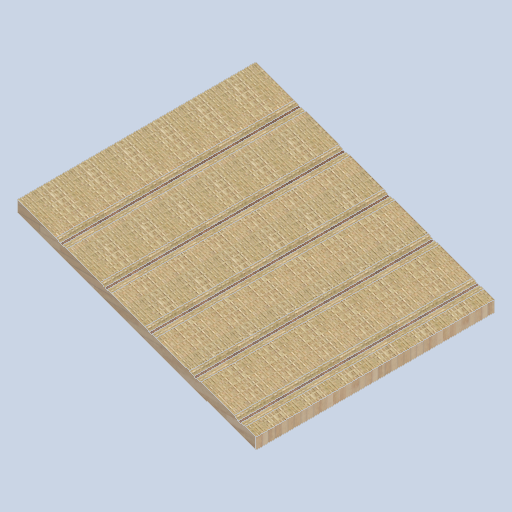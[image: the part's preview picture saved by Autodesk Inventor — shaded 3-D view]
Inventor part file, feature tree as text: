
AUTODESK INVENTOR PART (.ipt)
format: ipt  version: 2024.2 (Build 282272000, 272)  size: 355,840 bytes
history: native  units: in
note: dims shown in document units (in); Inventor stores cm internally (conversion verified against a paired STEP export)
features: other x3, sketch x3, plane x3
ambient origin geometry x8: Origin, YZ Plane, XZ Plane, XY Plane, X Axis, Y Axis, Z Axis, Center Point
bodies: Solid1 (feature_tree)
feature tree (9):
  other  "side_curve_panel_01_MIR.ipt"
  other  "Solid1::side_curve_panel_01_MIR.ipt"
  other  "TaggingFeature1"
  sketch  "Sketch1"  dims[d0=0.3937in]
  sketch  "Sketch4"
  sketch  "Sketch5"
  plane  "Work Plane1"
  plane  "Work Plane2"
  plane  "Work Plane3"
